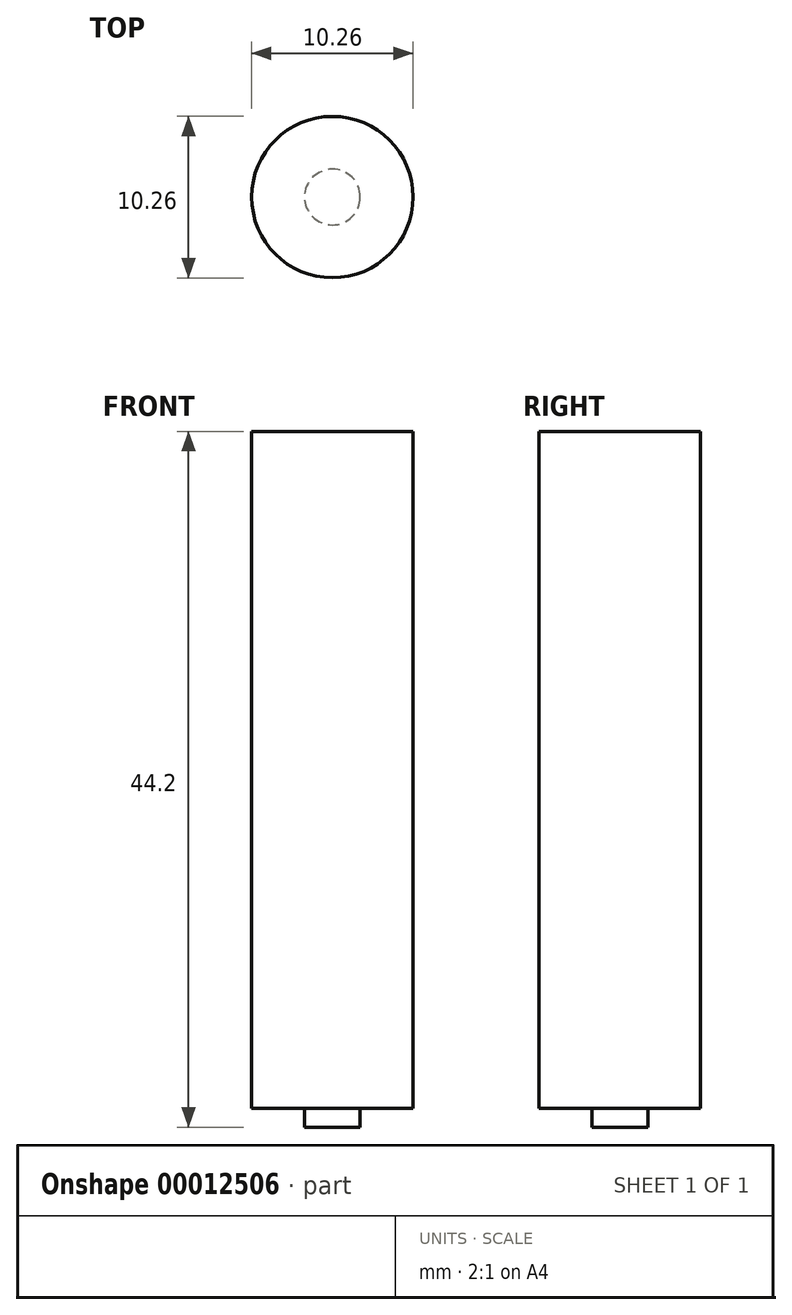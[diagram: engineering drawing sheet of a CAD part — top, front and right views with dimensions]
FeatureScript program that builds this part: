
annotation { "Feature Type Name" : "Feature", "Feature Type Description" : "" }
export const myFeature = defineFeature(function(context is Context, id is Id, definition is map)
    precondition{}
    {
        {
            var Q0;
            Q0=qCreatedBy(makeId("Top.planeOp"),FACE);
            var sketch = newSketch(context, id + "F0", { "sketchPlane" : qUnion([Q0])});
            skCircle(sketch, "E0", {"center": v(0, 0) * mm, "radius": 5.12 * mm});
            skCircle(sketch, "E1", {"center": v(0, 0) * mm, "radius": 1.77 * mm});
            skSolve(sketch);
        }
        {
            var Q0;
            Q0 = qSketchRegion(id + "F0", true);
            var Q1;
            Q1=makeQuery(id+"F0.imprint","IMPRINT",FACE,{"disambiguationData":[TD([[makeQuery(id+"F0.imprint","IMPRINT",EDGE,{"derivedFrom":sQuery(id+"F0.wireOp",EDGE,"E1")}),1.0]])]});
            extrude(context, id + "F1", {"entities" : qUnion([Q0, Q1]), "depth" : 43 * mm});
        }
        {
            var Q0;
            Q0=makeQuery(id+"F0.imprint","IMPRINT",FACE,{"disambiguationData":[TD([[makeQuery(id+"F0.imprint","IMPRINT",EDGE,{"derivedFrom":sQuery(id+"F0.wireOp",EDGE,"E1")}),1.0]])]});
            extrude(context, id + "F2", {"entities" : qUnion([Q0]), "operationType" : NewBodyOperationType.ADD, "oppositeDirection" : true, "depth" : 1.2 * mm});
        }
    });
